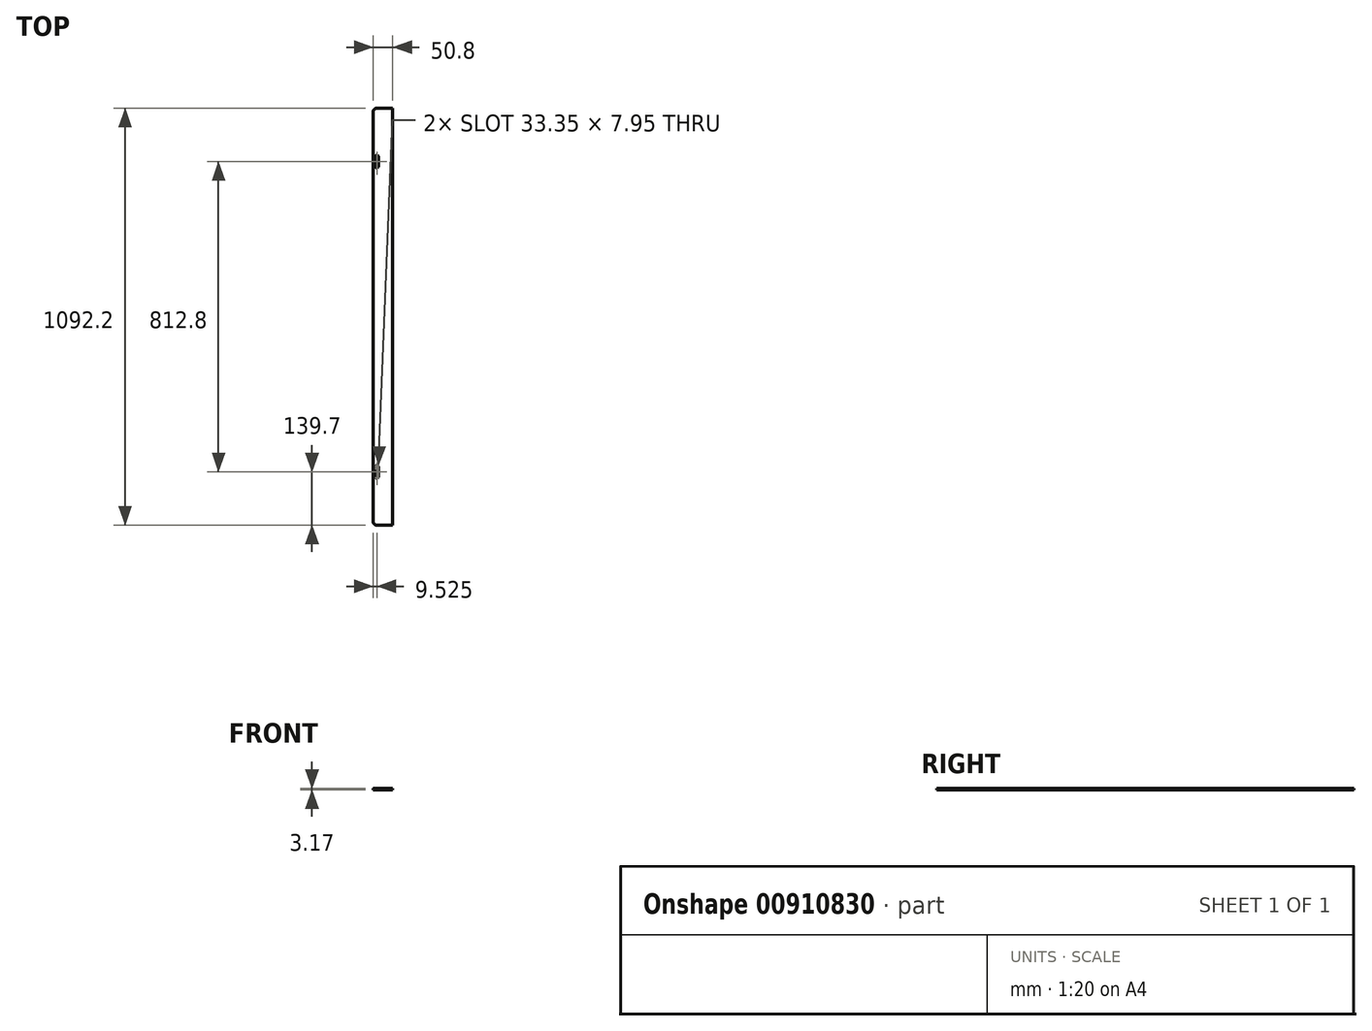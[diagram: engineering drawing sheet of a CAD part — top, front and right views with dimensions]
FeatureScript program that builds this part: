
annotation { "Feature Type Name" : "Feature", "Feature Type Description" : "" }
export const myFeature = defineFeature(function(context is Context, id is Id, definition is map)
    precondition{}
    {
        {
            var Q0;
            Q0=qCreatedBy(makeId("Front.planeOp"),FACE);
            var sketch = newSketch(context, id + "F0", { "sketchPlane" : qUnion([Q0])});
            skLineSegment(sketch, "E0.bottom", {"start": v(0, 0) * mm, "end": v(50.8, 0) * mm});
            skLineSegment(sketch, "E0.top", {"start": v(0, 3.18) * mm, "end": v(50.8, 3.18) * mm});
            skLineSegment(sketch, "E0.left", {"start": v(0, 0) * mm, "end": v(0, 3.18) * mm});
            skLineSegment(sketch, "E0.right", {"start": v(50.8, 0) * mm, "end": v(50.8, 3.18) * mm});
            skSolve(sketch);
        }
        {
            var Q0;
            Q0 = qSketchRegion(id + "F0", true);
            extrude(context, id + "F1", {"entities" : qUnion([Q0]), "flatOperationType" : FlatOperationType.REMOVE, "depth" : 1092.2 * mm, "offsetDistance" : 25.4 * mm, "domain" : OperationDomain.MODEL});
        }
        {
            var Q0;
            Q0=makeQuery(id+"F1.opExtrude","SWEPT_FACE",FACE,{"disambiguationData":[OSD([sQuery(id+"F0.wireOp",EDGE,"E0.top")])]});
            var sketch = newSketch(context, id + "F2", { "sketchPlane" : qUnion([Q0])});
            skArc(sketch, "E1", {"start": v(13.5, -127) * mm, "mid": v(9.52, -123.02) * mm, "end": v(5.55, -127) * mm});
            skArc(sketch, "E2", {"start": v(5.55, -152.4) * mm, "mid": v(9.53, -156.38) * mm, "end": v(13.5, -152.4) * mm});
            skArc(sketch, "E3", {"start": v(13.5, -939.8) * mm, "mid": v(9.52, -935.82) * mm, "end": v(5.55, -939.8) * mm});
            skArc(sketch, "E4", {"start": v(5.55, -965.2) * mm, "mid": v(9.53, -969.18) * mm, "end": v(13.5, -965.2) * mm});
            skLineSegment(sketch, "E5", {"start": v(5.55, -127) * mm, "end": v(5.55, -152.4) * mm});
            skLineSegment(sketch, "E6", {"start": v(13.5, -127) * mm, "end": v(13.5, -152.4) * mm});
            skLineSegment(sketch, "E7", {"start": v(5.55, -939.8) * mm, "end": v(5.55, -965.2) * mm});
            skLineSegment(sketch, "E8", {"start": v(13.5, -965.2) * mm, "end": v(13.5, -939.8) * mm});
            skSolve(sketch);
        }
        {
            var Q0;
            Q0 = qSketchRegion(id + "F2", true);
            extrude(context, id + "F3", {"entities" : qUnion([Q0]), "operationType" : NewBodyOperationType.REMOVE, "flatOperationType" : FlatOperationType.REMOVE, "endBound" : BoundingType.THROUGH_ALL, "oppositeDirection" : true, "depth" : 25.4 * mm, "offsetDistance" : 25.4 * mm, "domain" : OperationDomain.MODEL});
        }
        {
            var Q0;
            Q0=makeQuery(id+"F1.opExtrude","CAP_EDGE",EDGE,{"disambiguationData":[OSD([sQuery(id+"F0.wireOp",EDGE,"E0.left")])],"isStart":false});
            var Q1;
            Q1=makeQuery(id+"F1.opExtrude","CAP_EDGE",EDGE,{"disambiguationData":[OSD([sQuery(id+"F0.wireOp",EDGE,"E0.left")])],"isStart":true});
            fillet(context, id + "F4", {"entities" : qUnion([Q0, Q1]), "radius" : 9.52 * mm, "tangentPropagation" : true, "allowEdgeOverflow" : false});
        }
    });
